# Revit family: Plumbing_Fixture-Bathtub-BainUltra-Monarch-6030
name_source: partatom
category: Plumbing Fixtures
units: mm (PartAtom-declared; Revit-internal decimal feet)

## family parameters
Always vertical = Yes
Cut with Voids When Loaded = No
OmniClass Number = 23.45.05.17.17
OmniClass Title = Leisure Whirlpools
Part Type = Normal
Room Calculation Point = No
Round Connector Dimension = Use Radius
Shared = No
Work Plane-Based = No

## types (1)
- 60" x 30"
    Apparent Load = 0 VA
    Assembly Code = D2010510
    Capacity = 50
    Connector Description = ELECTRICAL CONNECTOR
    Country = UNITED STATES
    Default Elevation = 0' - 0"
    Description = Monarch baths feature radiant, sumptuous quartz deck surfaces in carefully selected enchanting colors combined with the bath inner shell made of 100% pure acrylic of the highest quality.
    Drain Connector Description = SANITARY DRAIN CONNECTION - Schedule 40
    Drain Diameter = 0' - 1 1/2"
    Drain Radius = 0' - 0 3/4"
    Height = 1' - 7 3/8"
    Jets = Yes
    LED Type = 2-Color Changing LEDs
    Length = 5' - 0"
    Load Classification = Lighting
    Manufacturer = BAINULTRA
    Model = 6030
    Number of Bathers = 1
    Number of Poles = 1
    Other Region = No
    Power Factor = 1
    Product Documentation Link = http://www.bainultra.com
    Product Name = MONARCH
    Product Page URL = http://www.bainultra.com
    Product data url = https://bimobject.com
    Region = NORTH AMERICA
    Series = MONARCH
    Shipping Weight = 226 lb
    URL = www.bainultra.com
    US Region = Yes
    Voltage = 120 V
    WFU = 1
    Water Flow = 0 GPM
    Width = 2' - 6"

## geometry (parser evidence)
native form markers: Blend x4, Sweep x9
no freeform markers — native parametric forms only
